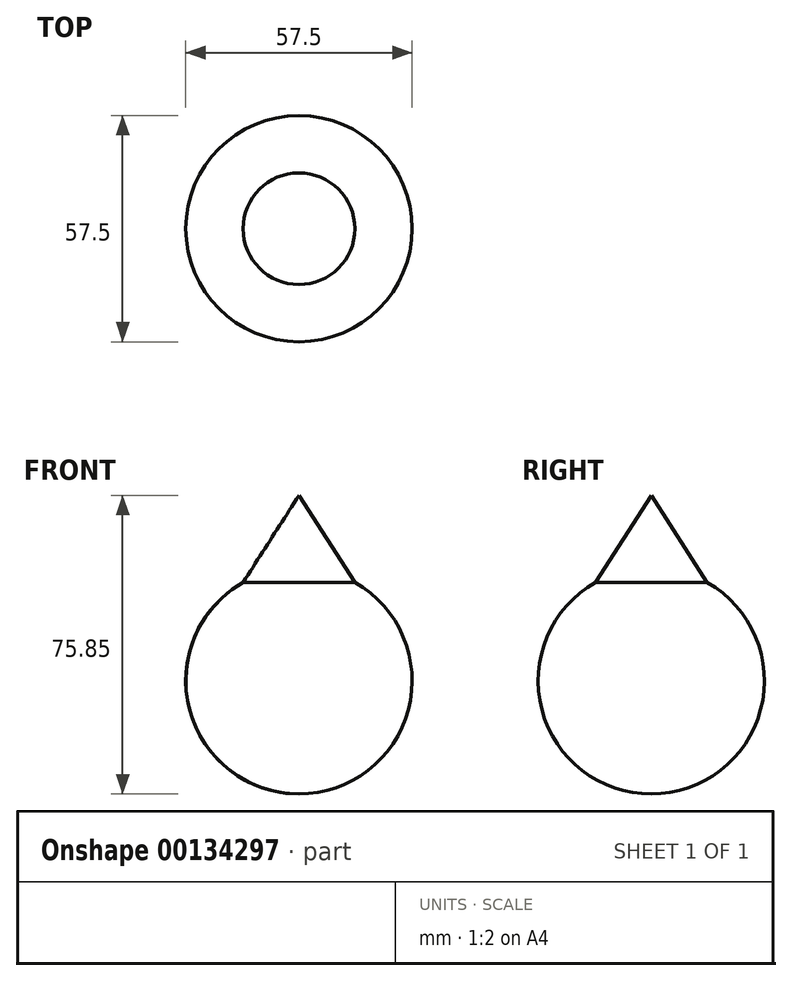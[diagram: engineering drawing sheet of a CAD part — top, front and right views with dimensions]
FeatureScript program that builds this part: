
annotation { "Feature Type Name" : "Feature", "Feature Type Description" : "" }
export const myFeature = defineFeature(function(context is Context, id is Id, definition is map)
    precondition{}
    {
        {
            var Q0;
            Q0=qCreatedBy(makeId("Front.planeOp"),FACE);
            var sketch = newSketch(context, id + "F0", { "sketchPlane" : qUnion([Q0])});
            skArc(sketch, "E0", {"start": v(0, 28.75) * mm, "mid": v(-28.75, 0) * mm, "end": v(0, -28.75) * mm});
            skLineSegment(sketch, "E1", {"start": v(0, 25) * mm, "end": v(-14.19, 25) * mm});
            skLineSegment(sketch, "E2", {"start": v(-14.19, 25) * mm, "end": v(0, 47.1) * mm});
            skLineSegment(sketch, "E3", {"start": v(0, 47.1) * mm, "end": v(0, -28.75) * mm});
            skLineSegment(sketch, "E4", {"start": v(0, 62.46) * mm, "end": v(0, -44.3) * mm});
            skSolve(sketch);
        }
        {
            var Q0;
            {var subQ3=sQuery(id+"F0.wireOp",EDGE,"E2");Q0=makeQuery(id+"F0.imprint","IMPRINT",FACE,{"disambiguationData":[TD([[makeQuery(id+"F0.imprint","IMPRINT",EDGE,{"derivedFrom":subQ3}),-1.0]])]});}
            var Q1;
            {var subQ3=sQuery(id+"F0.wireOp",EDGE,"E1");Q1=makeQuery(id+"F0.imprint","IMPRINT",FACE,{"disambiguationData":[TD([[makeQuery(id+"F0.imprint","IMPRINT",EDGE,{"derivedFrom":subQ3}),-1.0]])]});}
            var Q2;
            {var subQ3=sQuery(id+"F0.wireOp",EDGE,"E1");Q2=makeQuery(id+"F0.imprint","IMPRINT",FACE,{"disambiguationData":[TD([[makeQuery(id+"F0.imprint","IMPRINT",EDGE,{"derivedFrom":subQ3}),1.0]])]});}
            var Q3;
            Q3=sQuery(id+"F0.wireOp",EDGE,"E4");
            revolve(context, id + "F1", {"entities" : qUnion([Q0, Q1, Q2]), "axis" : qUnion([Q3]), "revolveType" : RevolveType.FULL});
        }
    });
